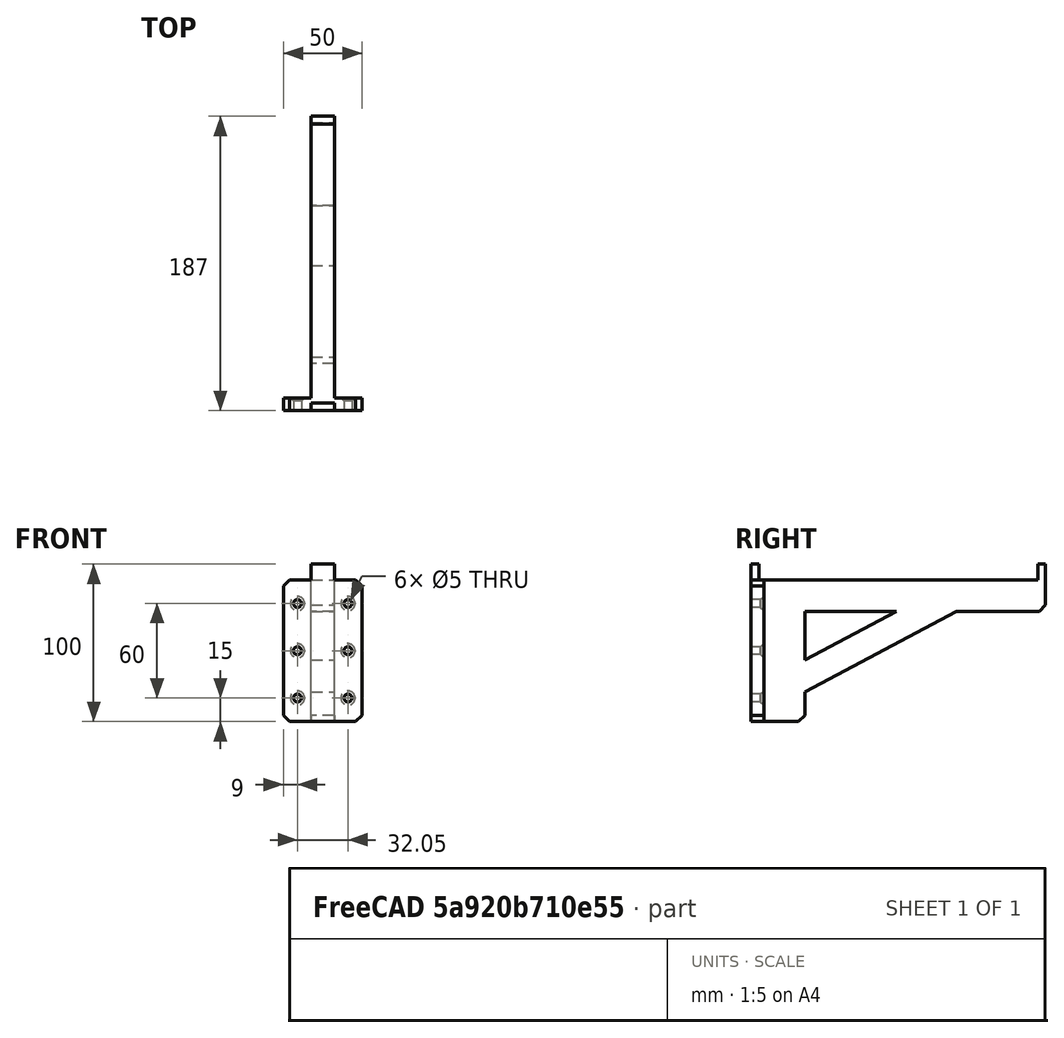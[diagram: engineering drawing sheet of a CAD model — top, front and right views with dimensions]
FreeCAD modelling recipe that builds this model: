
FCSTD DOCUMENT  (FreeCAD 0.18R16117 (Git))
Label: bracket-177mm
License: All rights reserved
LicenseURL: http://en.wikipedia.org/wiki/All_rights_reserved
objects: Part::Cylinder×6, Part::Box×5, Part::Cut×3, Part::Chamfer×3, Part::Fuse×1, Part::Compound×1, Part::MultiFuse×1
note: 20 computed .brp shape members not serialized (recipe doc carries the construction recipe); baked Part::Feature solids carry a one-line shape summary decoded from their .brp

FEATURE [Part::Box] Box  label="Cube"
  AttacherType = Attacher::AttachEngine3D
  Height = 100
  Length = 15
  Width = 187
FEATURE [Part::Box] Box001  label="Cube001"
  AttacherType = Attacher::AttachEngine3D
  Height = 100
  Length = 15
  Placement = pos=(0,34,-30) rot=(0,0,1;0rad)
  Width = 163
FEATURE [Part::Box] Box002  label="Cube002"
  AttacherType = Attacher::AttachEngine3D
  Height = 100
  Length = 15
  Placement = pos=(0,5,90) rot=(0,0,1;0rad)
  Width = 177
FEATURE [Part::Box] Box003  label="Cube003"
  AttacherType = Attacher::AttachEngine3D
  Height = 18
  Length = 15
  Placement = pos=(0,20,11.25) rot=(1,0,0;0.488692rad)
  Width = 125
FEATURE [Part::Cut] Cut
  Base = -> Box
  Tool = -> Box001
FEATURE [Part::Fuse] Fusion
  Base = -> Cut
  Tool = -> Box003
FEATURE [Part::Box] Box004  label="Cube004"
  AttacherType = Attacher::AttachEngine3D
  Height = 90
  Length = 50
  Placement = pos=(-17.5,0,0) rot=(0,0,1;0rad)
  Width = 8
FEATURE [Part::Chamfer] Chamfer
  Base = -> Box004
  Edges = 4 edges r=4: [Edge2,Edge4,Edge6,Edge8]
FEATURE [Part::Cylinder] Cylinder
  Angle = 360
  AttacherType = Attacher::AttachEngine3D
  Height = 20
  Placement = pos=(23.55,14,15) rot=(1,0,0;1.5708rad)
  Radius = 2.5
FEATURE [Part::Cylinder] Cylinder001
  Angle = 360
  AttacherType = Attacher::AttachEngine3D
  Height = 20
  Placement = pos=(-8.5,14,15) rot=(1,0,0;1.5708rad)
  Radius = 2.5
FEATURE [Part::Cylinder] Cylinder002
  Angle = 360
  AttacherType = Attacher::AttachEngine3D
  Height = 20
  Placement = pos=(23.55,14,45) rot=(1,0,0;1.5708rad)
  Radius = 2.5
FEATURE [Part::Cylinder] Cylinder004
  Angle = 360
  AttacherType = Attacher::AttachEngine3D
  Height = 20
  Placement = pos=(23.55,14,75) rot=(1,0,0;1.5708rad)
  Radius = 2.5
FEATURE [Part::Cylinder] Cylinder005
  Angle = 360
  AttacherType = Attacher::AttachEngine3D
  Height = 20
  Placement = pos=(-8.5,14,75) rot=(1,0,0;1.5708rad)
  Radius = 2.5
FEATURE [Part::Cylinder] Cylinder003
  Angle = 360
  AttacherType = Attacher::AttachEngine3D
  Height = 20
  Placement = pos=(-8.5,14,45) rot=(1,0,0;1.5708rad)
  Radius = 2.5
FEATURE [Part::Compound] Compound
  Links = -> [Cylinder,Cylinder001,Cylinder002,Cylinder004,Cylinder005,Cylinder003]
FEATURE [Part::Cut] Cut001
  Base = -> Chamfer
  Tool = -> Compound
FEATURE [Part::Cut] Cut002
  Base = -> Fusion
  Tool = -> Box002
FEATURE [Part::Chamfer] Chamfer001  label="Backplate"
  Base = -> Cut001
  Edges = 6 edges r=2: [Edge27,Edge28,Edge29,Edge30,Edge31,Edge32]
FEATURE [Part::Chamfer] Chamfer002  label="Arm"
  Base = -> Cut002
  Edges = 2 edges r=4: [Edge23,Edge33]
FEATURE [Part::MultiFuse] Fusion001  label="Final"
  Shapes = -> [Chamfer002,Chamfer001]
